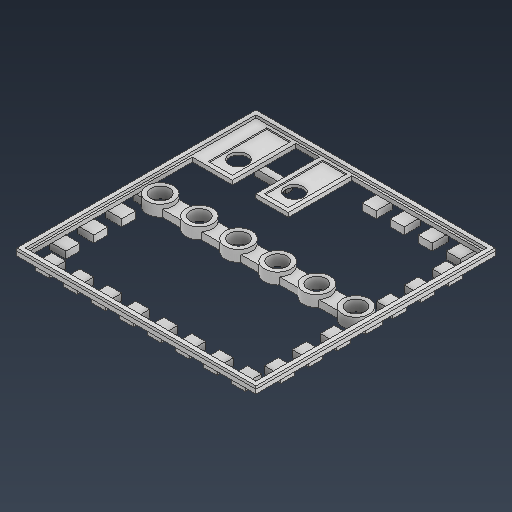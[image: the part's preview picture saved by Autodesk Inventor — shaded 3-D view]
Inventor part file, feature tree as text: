
AUTODESK INVENTOR PART (.ipt)
format: ipt  version: 2025.3 (Build 293356000, 356)  size: 875,520 bytes
history: native  units: mm
features: projected_geometry x26, sketch x20, extrude x8, fillet x1
ambient origin geometry x8: Origin, YZ Plane, XZ Plane, XY Plane, X Axis, Y Axis, Z Axis, Center Point
bodies: Solid1 (feature_tree), Solid2 (feature_tree)
feature tree (55):
  extrude  "Extrusion1"  Depth=171.0mm
  extrude  "Extrusion3"  Depth=60.0mm
  extrude  "Extrusion5"  Depth=78.0mm
  extrude  "Extrusion6"  Depth=75.0mm
  extrude  "Extrusion7"  Depth=30.0mm
  extrude  "Extrusion8"  Depth=5.0mm
  extrude  "Extrusion9"  Depth=5.0mm
  fillet  "Fillet1"  Radius=25.0mm
  extrude  "Extrusion10"  Depth=15.4mm
  sketch  "Sketch1"  dims[d0=171.0mm d1=171.0mm]
  sketch  "Sketch3"  dims[d10=78.0mm d11=78.0mm]
  sketch  "Sketch Rectangular Pattern1"  dims[d2=3.0mm d3=0.0mm d9=60.0mm]
  sketch  "Sketch Rectangular Pattern4"  dims[d12=60.0mm d17=75.0mm]
  sketch  "Sketch5"  dims[d20=5.0mm d21=30.0mm]
  sketch  "Sketch7"  dims[d32=15.4mm d33=15.4mm]
  projected_geometry  "Projected Loop3"
  sketch  "Sketch Rectangular Pattern5"  dims[d22=5.0mm d23=5.0mm]
  sketch  "Sketch8"  dims[d43=12.6mm]
  projected_geometry  "Projected Loop4"
  sketch  "Sketch Rectangular Pattern6"  dims[d27=5.0mm d28=5.0mm d31=25.0mm]
  sketch  "Sketch Rectangular Pattern7"  dims[d35=20.0mm d37=28.0mm d38=30.0mm d40=25.0mm]
  sketch  "Sketch Rectangular Pattern9"  dims[d44=6.3mm]
  sketch  "Sketch9"  dims[d45=4.0mm]
  projected_geometry  "Projected Loop5"
  projected_geometry  "Projected Loop6"
  projected_geometry  "Projected Loop7"
  projected_geometry  "Projected Loop8"
  projected_geometry  "Projected Loop9"
  projected_geometry  "Projected Loop10"
  projected_geometry  "Projected Loop11"
  projected_geometry  "Projected Loop12"
  sketch  "Sketch Rectangular Pattern11"  dims[d47=11.7mm]
  sketch  "Sketch Rectangular Pattern15"  dims[d52=15.4mm d53=15.4mm d54=28.0mm d55=25.0mm]
  projected_geometry  "Projected Loop26"
  projected_geometry  "Projected Loop27"
  projected_geometry  "Projected Loop28"
  projected_geometry  "Projected Loop29"
  projected_geometry  "Projected Loop30"
  projected_geometry  "Projected Loop31"
  projected_geometry  "Projected Loop32"
  projected_geometry  "Projected Loop33"
  projected_geometry  "Projected Loop34"
  projected_geometry  "Projected Loop35"
  projected_geometry  "Projected Loop36"
  projected_geometry  "Projected Loop37"
  projected_geometry  "Projected Loop38"
  projected_geometry  "Projected Loop39"
  projected_geometry  "Projected Loop40"
  projected_geometry  "Projected Loop41"
  sketch  "Sketch Rectangular Pattern16"  dims[d56=12.6mm]
  sketch  "Sketch Rectangular Pattern17"  dims[d57=30.0mm]
  sketch  "Sketch Rectangular Pattern18"  dims[d58=80.0mm]
  sketch  "Sketch Rectangular Pattern19"  dims[d59=25.0mm d60=25.0mm d61=20.0mm d62=40.0mm d63=8.0mm d64=8.0mm d65=10.0mm d66=0.0mm d67=80.0mm d68=16.2mm d69=16.2mm d70=16.2mm d71=28.0mm d72=28.0mm d73=12.0mm d74=12.8mm d75=12.8mm d76=12.8mm d77=13.0mm d78=60.0mm d80=28.0mm d81=10.0mm d83=10.0mm d85=11.5mm d86=163.0mm d87=65.0mm d88=95.0mm d89=88.0mm d90=13.0mm d91=13.0mm d92=30.0mm d93=40.0mm d94=17.5mm d99=13.0mm d100=28.8mm d101=17.2mm d102=17.2mm d103=1.0mm d104=0.0mm d105=4.0mm d106=4.0mm d107=4.0mm d108=4.0mm d109=4.0mm d110=4.0mm d111=7.0mm d112=4.0mm d113=4.0mm d114=4.0mm d115=4.5mm d116=5.0mm d117=22.0mm d118=12.0mm d119=6.0mm d120=10.0mm d121=0.0mm d122=3.0mm d123=60.0mm d125=28.0mm d126=10.0mm d128=10.0mm d130=3.0mm d131=3.0mm d132=3.0mm d133=3.0mm d134=3.0mm d135=10.0mm d136=6.0mm d137=80.0mm d139=20.0mm d140=10.0mm d142=10.0mm d145=10.0mm d146=40.0mm d148=20.0mm d149=10.0mm d151=10.0mm d153=16.0mm d154=10.0mm d162=10.0mm d163=16.0mm d164=5.0mm d165=0.0mm d166=30.0mm d168=20.0mm d169=10.0mm d171=10.0mm d181=10.0mm d182=80.0mm d184=20.0mm d185=10.0mm d187=10.0mm d215=10.0mm d216=0.0mm d217=6.0mm d218=70.0mm d220=20.0mm d221=10.0mm d223=10.0mm d225=10.0mm d226=10.0mm d227=10.0mm d228=10.0mm d229=10.0mm d230=10.0mm d231=10.0mm d232=10.0mm d233=30.0mm d235=20.0mm d236=10.0mm d238=10.0mm d240=40.0mm d242=20.0mm d243=10.0mm d245=10.0mm d247=30.0mm d249=20.0mm d250=10.0mm d252=10.0mm d254=30.0mm d256=20.0mm d257=10.0mm d259=10.0mm d261=2.7mm d262=10.0mm d263=0.0mm d264=1.0mm d265=3.0mm d266=2.0mm d267=0.0mm]
  sketch  "Sketch10"  dims[d46=14.0mm]
  sketch  "Sketch11"  dims[d49=20.0mm d51=30.0mm]
